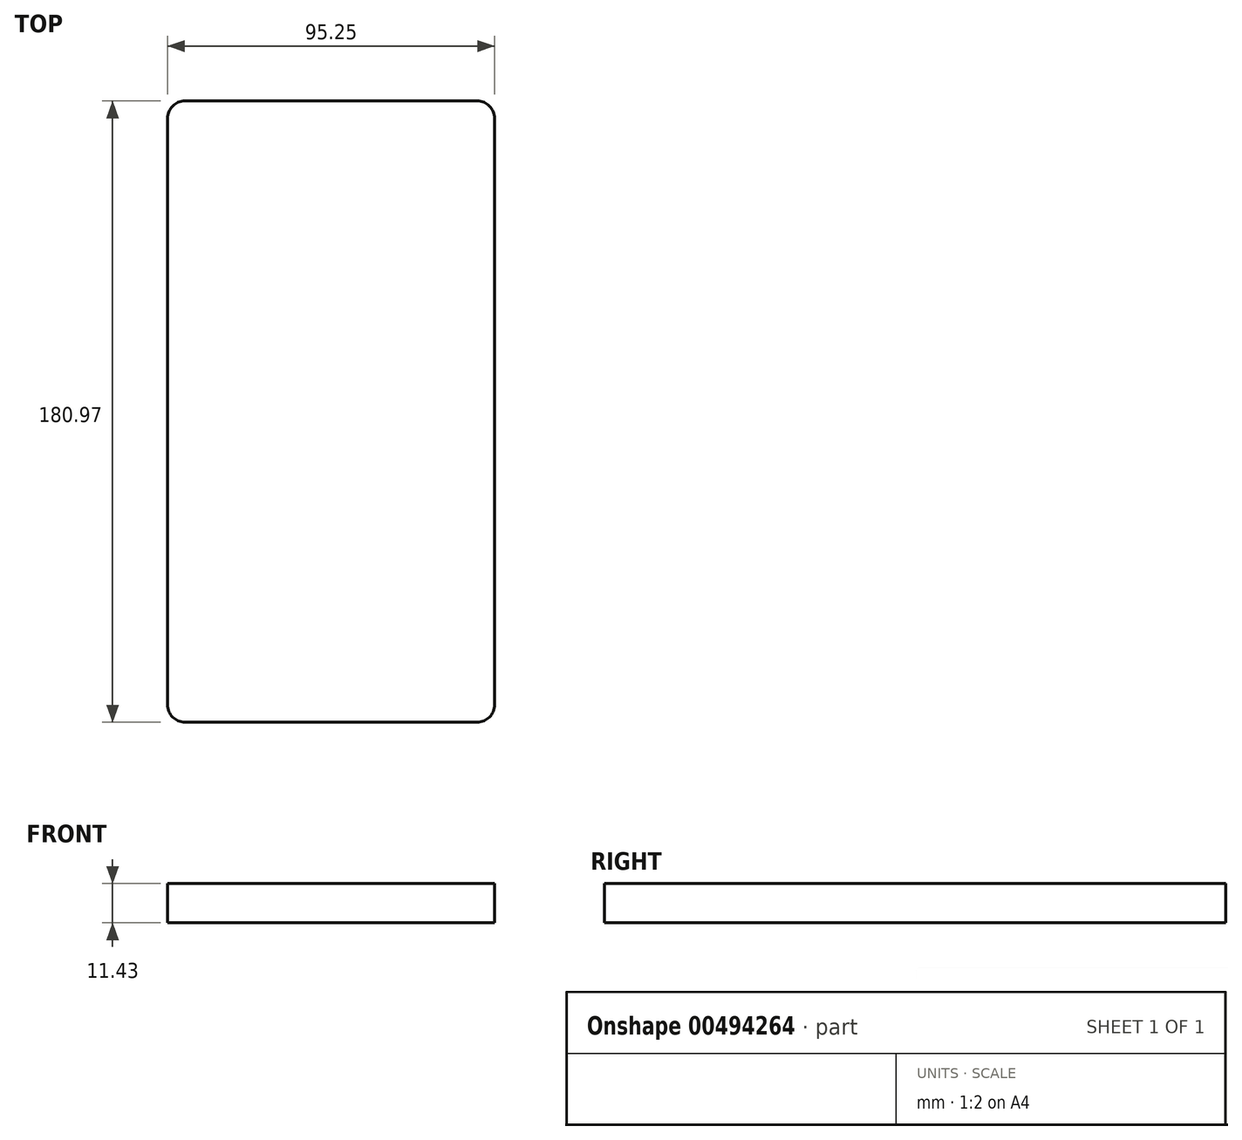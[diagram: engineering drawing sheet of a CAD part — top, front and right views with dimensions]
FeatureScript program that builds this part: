
annotation { "Feature Type Name" : "Feature", "Feature Type Description" : "" }
export const myFeature = defineFeature(function(context is Context, id is Id, definition is map)
    precondition{}
    {
        {
            var Q0;
            Q0=qCreatedBy(makeId("Top.planeOp"),FACE);
            var sketch = newSketch(context, id + "F0", { "sketchPlane" : qUnion([Q0])});
            skLineSegment(sketch, "E0.bottom", {"start": v(0, 180.98) * mm, "end": v(95.25, 180.98) * mm});
            skLineSegment(sketch, "E0.top", {"start": v(0, 0) * mm, "end": v(95.25, 0) * mm});
            skLineSegment(sketch, "E0.left", {"start": v(0, 180.98) * mm, "end": v(0, 0) * mm});
            skLineSegment(sketch, "E0.right", {"start": v(95.25, 180.98) * mm, "end": v(95.25, 0) * mm});
            skSolve(sketch);
        }
        {
            var Q0;
            Q0=qSketchRegion(id+"F0",true);
            extrude(context, id + "F1", {"entities" : qUnion([Q0]), "depth" : 11.43 * mm});
        }
        {
            var Q0;
            Q0=makeQuery(id+"F1.opExtrude","SWEPT_EDGE",EDGE,{"disambiguationData":[OSD([sQuery(id+"F0.wireOp",EDGE,"E0.top"),sQuery(id+"F0.wireOp",EDGE,"E0.left")])]});
            var Q1;
            Q1=makeQuery(id+"FRSx4ZBp6vqH2Ow_1.boolean.opBoolean","COPY",EDGE,{"derivedFrom":makeQuery(id+"FRSx4ZBp6vqH2Ow_1.opExtrude","SWEPT_EDGE",EDGE,{"disambiguationData":[OSD([sQuery(id+"FiVfZ3CO7zQEQTI_1.wireOp",EDGE,"rLw3rtFq-aquM-BWbu-SVol-WMDXMmRNdKNx.top"),sQuery(id+"FiVfZ3CO7zQEQTI_1.wireOp",EDGE,"rLw3rtFq-aquM-BWbu-SVol-WMDXMmRNdKNx.right")])]})});
            var Q2;
            Q2=makeQuery(id+"F1.opExtrude","SWEPT_EDGE",EDGE,{"disambiguationData":[OSD([sQuery(id+"F0.wireOp",EDGE,"E0.top"),sQuery(id+"F0.wireOp",EDGE,"E0.right")])]});
            var Q3;
            Q3=makeQuery(id+"FRSx4ZBp6vqH2Ow_1.boolean.opBoolean","COPY",EDGE,{"derivedFrom":makeQuery(id+"FRSx4ZBp6vqH2Ow_1.opExtrude","SWEPT_EDGE",EDGE,{"disambiguationData":[OSD([sQuery(id+"FiVfZ3CO7zQEQTI_1.wireOp",EDGE,"rLw3rtFq-aquM-BWbu-SVol-WMDXMmRNdKNx.top"),sQuery(id+"FiVfZ3CO7zQEQTI_1.wireOp",EDGE,"rLw3rtFq-aquM-BWbu-SVol-WMDXMmRNdKNx.left")])]})});
            var Q4;
            Q4=makeQuery(id+"FRSx4ZBp6vqH2Ow_1.boolean.opBoolean","COPY",EDGE,{"derivedFrom":makeQuery(id+"FRSx4ZBp6vqH2Ow_1.opExtrude","SWEPT_EDGE",EDGE,{"disambiguationData":[OSD([sQuery(id+"FiVfZ3CO7zQEQTI_1.wireOp",EDGE,"rLw3rtFq-aquM-BWbu-SVol-WMDXMmRNdKNx.bottom"),sQuery(id+"FiVfZ3CO7zQEQTI_1.wireOp",EDGE,"rLw3rtFq-aquM-BWbu-SVol-WMDXMmRNdKNx.right")])]})});
            var Q5;
            Q5=makeQuery(id+"FRSx4ZBp6vqH2Ow_1.boolean.opBoolean","COPY",EDGE,{"derivedFrom":makeQuery(id+"FRSx4ZBp6vqH2Ow_1.opExtrude","SWEPT_EDGE",EDGE,{"disambiguationData":[OSD([sQuery(id+"FiVfZ3CO7zQEQTI_1.wireOp",EDGE,"rLw3rtFq-aquM-BWbu-SVol-WMDXMmRNdKNx.bottom"),sQuery(id+"FiVfZ3CO7zQEQTI_1.wireOp",EDGE,"rLw3rtFq-aquM-BWbu-SVol-WMDXMmRNdKNx.left")])]})});
            var Q6;
            Q6=makeQuery(id+"FRSx4ZBp6vqH2Ow_1.boolean.opBoolean","COPY",EDGE,{"derivedFrom":makeQuery(id+"FRSx4ZBp6vqH2Ow_1.opExtrude","SWEPT_EDGE",EDGE,{"disambiguationData":[OSD([sQuery(id+"FiVfZ3CO7zQEQTI_1.wireOp",EDGE,"7wRUb051-3g3v-hB9a-DPfZ-sgu3cH5MRuOd.top"),sQuery(id+"FiVfZ3CO7zQEQTI_1.wireOp",EDGE,"7wRUb051-3g3v-hB9a-DPfZ-sgu3cH5MRuOd.right")])]})});
            var Q7;
            Q7=makeQuery(id+"FRSx4ZBp6vqH2Ow_1.boolean.opBoolean","COPY",EDGE,{"derivedFrom":makeQuery(id+"FRSx4ZBp6vqH2Ow_1.opExtrude","SWEPT_EDGE",EDGE,{"disambiguationData":[OSD([sQuery(id+"FiVfZ3CO7zQEQTI_1.wireOp",EDGE,"7wRUb051-3g3v-hB9a-DPfZ-sgu3cH5MRuOd.top"),sQuery(id+"FiVfZ3CO7zQEQTI_1.wireOp",EDGE,"7wRUb051-3g3v-hB9a-DPfZ-sgu3cH5MRuOd.left")])]})});
            var Q8;
            Q8=makeQuery(id+"F1.opExtrude","SWEPT_EDGE",EDGE,{"disambiguationData":[OSD([sQuery(id+"F0.wireOp",EDGE,"E0.bottom"),sQuery(id+"F0.wireOp",EDGE,"E0.left")])]});
            var Q9;
            Q9=makeQuery(id+"F1.opExtrude","SWEPT_EDGE",EDGE,{"disambiguationData":[OSD([sQuery(id+"F0.wireOp",EDGE,"E0.bottom"),sQuery(id+"F0.wireOp",EDGE,"E0.right")])]});
            var Q10;
            Q10=makeQuery(id+"FRSx4ZBp6vqH2Ow_1.boolean.opBoolean","COPY",EDGE,{"derivedFrom":makeQuery(id+"FRSx4ZBp6vqH2Ow_1.opExtrude","SWEPT_EDGE",EDGE,{"disambiguationData":[OSD([sQuery(id+"FiVfZ3CO7zQEQTI_1.wireOp",EDGE,"7wRUb051-3g3v-hB9a-DPfZ-sgu3cH5MRuOd.bottom"),sQuery(id+"FiVfZ3CO7zQEQTI_1.wireOp",EDGE,"7wRUb051-3g3v-hB9a-DPfZ-sgu3cH5MRuOd.right")])]})});
            var Q11;
            Q11=makeQuery(id+"FRSx4ZBp6vqH2Ow_1.boolean.opBoolean","COPY",EDGE,{"derivedFrom":makeQuery(id+"FRSx4ZBp6vqH2Ow_1.opExtrude","SWEPT_EDGE",EDGE,{"disambiguationData":[OSD([sQuery(id+"FiVfZ3CO7zQEQTI_1.wireOp",EDGE,"7wRUb051-3g3v-hB9a-DPfZ-sgu3cH5MRuOd.bottom"),sQuery(id+"FiVfZ3CO7zQEQTI_1.wireOp",EDGE,"7wRUb051-3g3v-hB9a-DPfZ-sgu3cH5MRuOd.left")])]})});
            fillet(context, id + "F2", {"entities" : qUnion([Q0, Q1, Q2, Q3, Q4, Q5, Q6, Q7, Q8, Q9, Q10, Q11]), "radius" : 5.08 * mm, "tangentPropagation" : true, "allowEdgeOverflow" : false});
        }
    });
